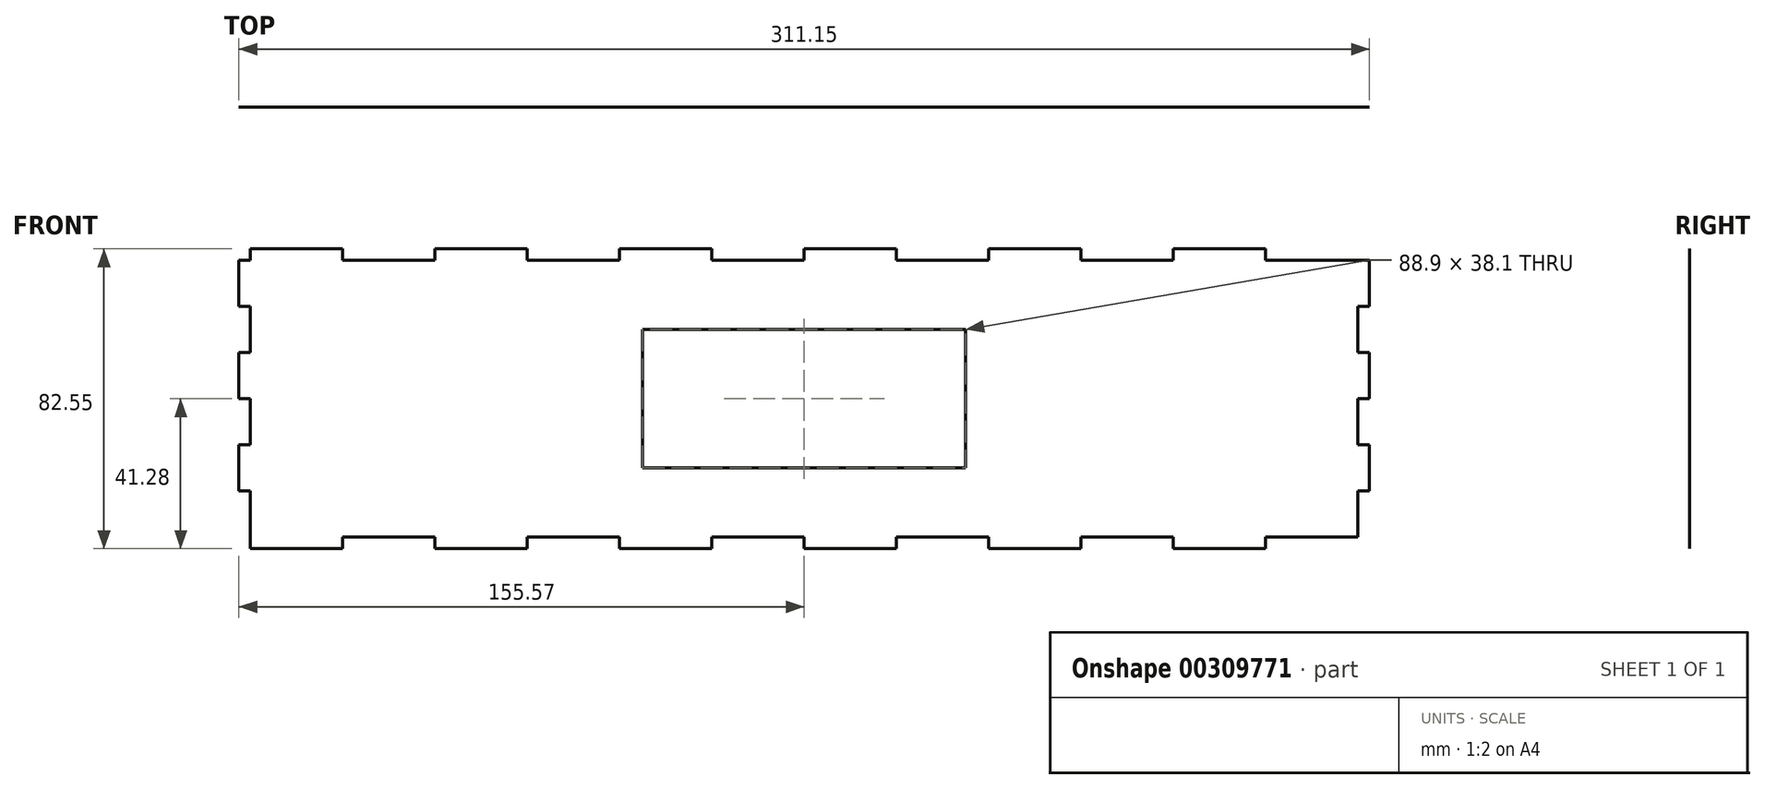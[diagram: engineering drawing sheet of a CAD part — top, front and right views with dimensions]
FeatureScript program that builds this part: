
annotation { "Feature Type Name" : "Feature", "Feature Type Description" : "" }
export const myFeature = defineFeature(function(context is Context, id is Id, definition is map)
    precondition{}
    {
        {
            var Q0;
            Q0=qCreatedBy(makeId("Front.planeOp"),FACE);
            var sketch = newSketch(context, id + "F0", { "sketchPlane" : qUnion([Q0])});
            skLineSegment(sketch, "E0.bottom", {"start": v(25.4, 0) * mm, "end": v(50.8, 0) * mm});
            skLineSegment(sketch, "E1.top", {"start": v(0, 3.18) * mm, "end": v(25.4, 3.18) * mm});
            skLineSegment(sketch, "E1.left", {"start": v(0, 0) * mm, "end": v(0, 3.18) * mm});
            skLineSegment(sketch, "E1.right", {"start": v(25.4, 0) * mm, "end": v(25.4, 3.18) * mm});
            skLineSegment(sketch, "E2.bottom", {"start": v(0, 0) * mm, "end": v(-3.17, 0) * mm});
            skLineSegment(sketch, "E2.top", {"start": v(0, -12.7) * mm, "end": v(-3.18, -12.7) * mm});
            skLineSegment(sketch, "E2.right", {"start": v(-3.18, 0) * mm, "end": v(-3.18, -12.7) * mm});
            skLineSegment(sketch, "E3.0.1.0", {"start": v(0, -25.4) * mm, "end": v(-3.17, -25.4) * mm});
            skLineSegment(sketch, "E3.0.1.1", {"start": v(-3.18, -25.4) * mm, "end": v(-3.18, -38.1) * mm});
            skLineSegment(sketch, "E3.0.1.2", {"start": v(0, -38.1) * mm, "end": v(-3.17, -38.1) * mm});
            skLineSegment(sketch, "E3.0.2.0", {"start": v(0, -50.8) * mm, "end": v(-3.17, -50.8) * mm});
            skLineSegment(sketch, "E3.0.2.1", {"start": v(-3.18, -50.8) * mm, "end": v(-3.18, -63.5) * mm});
            skLineSegment(sketch, "E3.0.2.2", {"start": v(0, -63.5) * mm, "end": v(-3.17, -63.5) * mm});
            skLineSegment(sketch, "E3.direction1", {"start": v(-3.17, 0) * mm, "end": v(0, 0) * mm, "construction": true});
            skLineSegment(sketch, "E3.direction2", {"start": v(-3.17, 0) * mm, "end": v(-3.17, -25.4) * mm, "construction": true});
            skLineSegment(sketch, "E4.1.0.0", {"start": v(50.8, 3.18) * mm, "end": v(76.2, 3.18) * mm});
            skLineSegment(sketch, "E4.1.0.1", {"start": v(50.8, 0) * mm, "end": v(50.8, 3.18) * mm});
            skLineSegment(sketch, "E4.1.0.2", {"start": v(76.2, 0) * mm, "end": v(76.2, 3.18) * mm});
            skLineSegment(sketch, "E4.2.0.0", {"start": v(101.6, 3.18) * mm, "end": v(127, 3.18) * mm});
            skLineSegment(sketch, "E4.2.0.1", {"start": v(101.6, 0) * mm, "end": v(101.6, 3.18) * mm});
            skLineSegment(sketch, "E4.2.0.2", {"start": v(127, 0) * mm, "end": v(127, 3.18) * mm});
            skLineSegment(sketch, "E4.3.0.0", {"start": v(152.4, 3.18) * mm, "end": v(177.8, 3.18) * mm});
            skLineSegment(sketch, "E4.3.0.1", {"start": v(152.4, 0) * mm, "end": v(152.4, 3.18) * mm});
            skLineSegment(sketch, "E4.3.0.2", {"start": v(177.8, 0) * mm, "end": v(177.8, 3.18) * mm});
            skLineSegment(sketch, "E4.4.0.0", {"start": v(203.2, 3.18) * mm, "end": v(228.6, 3.18) * mm});
            skLineSegment(sketch, "E4.4.0.1", {"start": v(203.2, 0) * mm, "end": v(203.2, 3.18) * mm});
            skLineSegment(sketch, "E4.4.0.2", {"start": v(228.6, 0) * mm, "end": v(228.6, 3.18) * mm});
            skLineSegment(sketch, "E4.5.0.0", {"start": v(254, 3.18) * mm, "end": v(279.4, 3.18) * mm});
            skLineSegment(sketch, "E4.5.0.1", {"start": v(254, 0) * mm, "end": v(254, 3.18) * mm});
            skLineSegment(sketch, "E4.5.0.2", {"start": v(279.4, 0) * mm, "end": v(279.4, 3.18) * mm});
            skLineSegment(sketch, "E4.direction1", {"start": v(0, 3.18) * mm, "end": v(50.8, 3.18) * mm, "construction": true});
            skLineSegment(sketch, "E5.trimOffspring", {"start": v(76.2, 0) * mm, "end": v(101.6, 0) * mm});
            skLineSegment(sketch, "E6.trimOffspring", {"start": v(127, 0) * mm, "end": v(152.4, 0) * mm});
            skLineSegment(sketch, "E7.trimOffspring", {"start": v(177.8, 0) * mm, "end": v(203.2, 0) * mm});
            skLineSegment(sketch, "E8.trimOffspring", {"start": v(228.6, 0) * mm, "end": v(254, 0) * mm});
            skLineSegment(sketch, "E9.trimOffspring", {"start": v(279.4, 0) * mm, "end": v(304.8, 0) * mm});
            skLineSegment(sketch, "E10.MirrorCS", {"start": v(307.98, 0) * mm, "end": v(307.98, -25.4) * mm, "construction": true});
            skLineSegment(sketch, "E11.MirrorCS", {"start": v(307.98, 0) * mm, "end": v(304.8, 0) * mm, "construction": true});
            skLineSegment(sketch, "E12.MirrorCS", {"start": v(304.8, -12.7) * mm, "end": v(307.98, -12.7) * mm});
            skLineSegment(sketch, "E13.MirrorCS", {"start": v(304.8, -25.4) * mm, "end": v(307.98, -25.4) * mm});
            skLineSegment(sketch, "E14.MirrorCS", {"start": v(307.98, -25.4) * mm, "end": v(307.98, -38.1) * mm});
            skLineSegment(sketch, "E15.MirrorCS", {"start": v(304.8, -38.1) * mm, "end": v(307.98, -38.1) * mm});
            skLineSegment(sketch, "E16.MirrorCS", {"start": v(304.8, -50.8) * mm, "end": v(307.98, -50.8) * mm});
            skLineSegment(sketch, "E17.MirrorCS", {"start": v(307.98, -50.8) * mm, "end": v(307.98, -63.5) * mm});
            skLineSegment(sketch, "E18.MirrorCS", {"start": v(304.8, -63.5) * mm, "end": v(307.98, -63.5) * mm});
            skLineSegment(sketch, "E19.trimOffspring", {"start": v(304.8, -38.1) * mm, "end": v(304.8, -50.8) * mm});
            skLineSegment(sketch, "E20.trimOffspring", {"start": v(304.8, -63.5) * mm, "end": v(304.8, -76.2) * mm});
            skLineSegment(sketch, "E21.trimOffspring", {"start": v(0, -38.1) * mm, "end": v(0, -50.8) * mm});
            skLineSegment(sketch, "E22.trimOffspring", {"start": v(0, -63.5) * mm, "end": v(0, -76.2) * mm});
            skLineSegment(sketch, "E23", {"start": v(0, -12.7) * mm, "end": v(0, -25.4) * mm});
            skLineSegment(sketch, "E24", {"start": v(304.8, -12.7) * mm, "end": v(304.8, -25.4) * mm});
            skLineSegment(sketch, "E25", {"start": v(307.98, 0) * mm, "end": v(307.98, -12.7) * mm});
            skLineSegment(sketch, "E26", {"start": v(307.98, 0) * mm, "end": v(304.8, 0) * mm});
            skLineSegment(sketch, "E27", {"start": v(25.4, -76.2) * mm, "end": v(50.8, -76.2) * mm});
            skLineSegment(sketch, "E28.MirrorCS", {"start": v(152.4, -79.38) * mm, "end": v(177.8, -79.38) * mm});
            skLineSegment(sketch, "E29.MirrorCS", {"start": v(203.2, -79.38) * mm, "end": v(228.6, -79.38) * mm});
            skLineSegment(sketch, "E30.MirrorCS", {"start": v(254, -79.38) * mm, "end": v(279.4, -79.38) * mm});
            skLineSegment(sketch, "E31.MirrorCS", {"start": v(101.6, -79.38) * mm, "end": v(127, -79.38) * mm});
            skLineSegment(sketch, "E32.MirrorCS", {"start": v(50.8, -79.38) * mm, "end": v(76.2, -79.38) * mm});
            skLineSegment(sketch, "E33.MirrorCS", {"start": v(25.4, -76.2) * mm, "end": v(25.4, -79.38) * mm});
            skLineSegment(sketch, "E34.MirrorCS", {"start": v(50.8, -76.2) * mm, "end": v(50.8, -79.38) * mm});
            skLineSegment(sketch, "E35.MirrorCS", {"start": v(76.2, -76.2) * mm, "end": v(76.2, -79.38) * mm});
            skLineSegment(sketch, "E36.MirrorCS", {"start": v(101.6, -76.2) * mm, "end": v(101.6, -79.38) * mm});
            skLineSegment(sketch, "E37.MirrorCS", {"start": v(127, -76.2) * mm, "end": v(127, -79.38) * mm});
            skLineSegment(sketch, "E38.MirrorCS", {"start": v(177.8, -76.2) * mm, "end": v(177.8, -79.38) * mm});
            skLineSegment(sketch, "E39.MirrorCS", {"start": v(152.4, -76.2) * mm, "end": v(152.4, -79.38) * mm});
            skLineSegment(sketch, "E40.MirrorCS", {"start": v(228.6, -76.2) * mm, "end": v(228.6, -79.38) * mm});
            skLineSegment(sketch, "E41.MirrorCS", {"start": v(203.2, -76.2) * mm, "end": v(203.2, -79.38) * mm});
            skLineSegment(sketch, "E42.MirrorCS", {"start": v(254, -76.2) * mm, "end": v(254, -79.38) * mm});
            skLineSegment(sketch, "E43.MirrorCS", {"start": v(279.4, -76.2) * mm, "end": v(279.4, -79.38) * mm});
            skLineSegment(sketch, "E44.MirrorCS", {"start": v(0, -76.2) * mm, "end": v(0, -79.38) * mm});
            skLineSegment(sketch, "E45", {"start": v(0, -79.38) * mm, "end": v(25.4, -79.38) * mm});
            skLineSegment(sketch, "E46.trimOffspring", {"start": v(76.2, -76.2) * mm, "end": v(101.6, -76.2) * mm});
            skLineSegment(sketch, "E47.trimOffspring", {"start": v(127, -76.2) * mm, "end": v(152.4, -76.2) * mm});
            skLineSegment(sketch, "E48.trimOffspring", {"start": v(177.8, -76.2) * mm, "end": v(203.2, -76.2) * mm});
            skLineSegment(sketch, "E49.trimOffspring", {"start": v(228.6, -76.2) * mm, "end": v(254, -76.2) * mm});
            skLineSegment(sketch, "E50.trimOffspring", {"start": v(279.4, -76.2) * mm, "end": v(304.8, -76.2) * mm});
            skSolve(sketch);
        }
        {
            var Q0;
            Q0=makeQuery(id+"F0.imprint","IMPRINT",FACE,{"disambiguationData":[TD([[makeQuery(id+"F0.imprint","IMPRINT",EDGE,{"derivedFrom":sQuery(id+"F0.wireOp",EDGE,"E0.bottom")}),-1.0]])]});
            var Q1;
            {var subQ4=sQuery(id+"F0.wireOp",EDGE,"E4.3.0.0");Q1=makeQuery(id+"F0.imprint","IMPRINT",FACE,{"disambiguationData":[TD([[makeQuery(id+"F0.imprint","IMPRINT",EDGE,{"derivedFrom":subQ4}),-1.0]])]});}
            var Q2;
            {var subQ6=sQuery(id+"F0.wireOp",EDGE,"E17.MirrorCS");Q2=makeQuery(id+"F0.imprint","IMPRINT",FACE,{"disambiguationData":[TD([[makeQuery(id+"F0.imprint","IMPRINT",EDGE,{"derivedFrom":subQ6}),-1.0]])]});}
            extrude(context, id + "F1", {"entities" : qUnion([Q0, Q1, Q2]), "depth" : 1 / 203.2 * mm});
        }
        {
            var Q0;
            Q0=makeQuery(id+"F1.opExtrude","CAP_FACE",FACE,{"disambiguationData":[OSD([sQuery(id+"F0.wireOp",EDGE,"E0.bottom"),sQuery(id+"F0.wireOp",EDGE,"E1.top"),sQuery(id+"F0.wireOp",EDGE,"E1.left"),sQuery(id+"F0.wireOp",EDGE,"E1.right"),sQuery(id+"F0.wireOp",EDGE,"E2.bottom"),sQuery(id+"F0.wireOp",EDGE,"E2.top"),sQuery(id+"F0.wireOp",EDGE,"E2.right"),sQuery(id+"F0.wireOp",EDGE,"E3.0.1.0"),sQuery(id+"F0.wireOp",EDGE,"E3.0.1.1"),sQuery(id+"F0.wireOp",EDGE,"E3.0.1.2"),sQuery(id+"F0.wireOp",EDGE,"E3.0.2.0"),sQuery(id+"F0.wireOp",EDGE,"E3.0.2.1"),sQuery(id+"F0.wireOp",EDGE,"E3.0.2.2"),sQuery(id+"F0.wireOp",EDGE,"E4.1.0.0"),sQuery(id+"F0.wireOp",EDGE,"E4.1.0.1"),sQuery(id+"F0.wireOp",EDGE,"E4.1.0.2"),sQuery(id+"F0.wireOp",EDGE,"E4.2.0.0"),sQuery(id+"F0.wireOp",EDGE,"E4.2.0.1"),sQuery(id+"F0.wireOp",EDGE,"E4.2.0.2"),sQuery(id+"F0.wireOp",EDGE,"E4.3.0.0"),sQuery(id+"F0.wireOp",EDGE,"E4.3.0.1"),sQuery(id+"F0.wireOp",EDGE,"E4.3.0.2"),sQuery(id+"F0.wireOp",EDGE,"E4.4.0.0"),sQuery(id+"F0.wireOp",EDGE,"E4.4.0.1"),sQuery(id+"F0.wireOp",EDGE,"E4.4.0.2"),sQuery(id+"F0.wireOp",EDGE,"E4.5.0.0"),sQuery(id+"F0.wireOp",EDGE,"E4.5.0.1"),sQuery(id+"F0.wireOp",EDGE,"E4.5.0.2"),sQuery(id+"F0.wireOp",EDGE,"E5.trimOffspring"),sQuery(id+"F0.wireOp",EDGE,"E6.trimOffspring"),sQuery(id+"F0.wireOp",EDGE,"E7.trimOffspring"),sQuery(id+"F0.wireOp",EDGE,"E8.trimOffspring"),sQuery(id+"F0.wireOp",EDGE,"E9.trimOffspring"),sQuery(id+"F0.wireOp",EDGE,"E12.MirrorCS"),sQuery(id+"F0.wireOp",EDGE,"E13.MirrorCS"),sQuery(id+"F0.wireOp",EDGE,"E14.MirrorCS"),sQuery(id+"F0.wireOp",EDGE,"E15.MirrorCS"),sQuery(id+"F0.wireOp",EDGE,"E16.MirrorCS"),sQuery(id+"F0.wireOp",EDGE,"E17.MirrorCS"),sQuery(id+"F0.wireOp",EDGE,"E18.MirrorCS"),sQuery(id+"F0.wireOp",EDGE,"E19.trimOffspring"),sQuery(id+"F0.wireOp",EDGE,"E20.trimOffspring"),sQuery(id+"F0.wireOp",EDGE,"E21.trimOffspring"),sQuery(id+"F0.wireOp",EDGE,"E22.trimOffspring"),sQuery(id+"F0.wireOp",EDGE,"E23"),sQuery(id+"F0.wireOp",EDGE,"E24"),sQuery(id+"F0.wireOp",EDGE,"E25"),sQuery(id+"F0.wireOp",EDGE,"E26"),sQuery(id+"F0.wireOp",EDGE,"E27"),sQuery(id+"F0.wireOp",EDGE,"E28.MirrorCS"),sQuery(id+"F0.wireOp",EDGE,"E29.MirrorCS"),sQuery(id+"F0.wireOp",EDGE,"E30.MirrorCS"),sQuery(id+"F0.wireOp",EDGE,"E31.MirrorCS"),sQuery(id+"F0.wireOp",EDGE,"E32.MirrorCS"),sQuery(id+"F0.wireOp",EDGE,"E33.MirrorCS"),sQuery(id+"F0.wireOp",EDGE,"E34.MirrorCS"),sQuery(id+"F0.wireOp",EDGE,"E35.MirrorCS"),sQuery(id+"F0.wireOp",EDGE,"E36.MirrorCS"),sQuery(id+"F0.wireOp",EDGE,"E37.MirrorCS"),sQuery(id+"F0.wireOp",EDGE,"E38.MirrorCS"),sQuery(id+"F0.wireOp",EDGE,"E39.MirrorCS"),sQuery(id+"F0.wireOp",EDGE,"E40.MirrorCS"),sQuery(id+"F0.wireOp",EDGE,"E41.MirrorCS"),sQuery(id+"F0.wireOp",EDGE,"E42.MirrorCS"),sQuery(id+"F0.wireOp",EDGE,"E43.MirrorCS"),sQuery(id+"F0.wireOp",EDGE,"E44.MirrorCS"),sQuery(id+"F0.wireOp",EDGE,"E45"),sQuery(id+"F0.wireOp",EDGE,"E46.trimOffspring"),sQuery(id+"F0.wireOp",EDGE,"E47.trimOffspring"),sQuery(id+"F0.wireOp",EDGE,"E48.trimOffspring"),sQuery(id+"F0.wireOp",EDGE,"E49.trimOffspring"),sQuery(id+"F0.wireOp",EDGE,"E50.trimOffspring")])],"isStart":false});
            var sketch = newSketch(context, id + "F2", { "sketchPlane" : qUnion([Q0])});
            skLineSegment(sketch, "E51.bottom", {"start": v(107.95, -19.05) * mm, "end": v(196.85, -19.05) * mm});
            skLineSegment(sketch, "E51.top", {"start": v(107.95, -57.15) * mm, "end": v(196.85, -57.15) * mm});
            skLineSegment(sketch, "E51.left", {"start": v(107.95, -19.05) * mm, "end": v(107.95, -57.15) * mm});
            skLineSegment(sketch, "E51.right", {"start": v(196.85, -19.05) * mm, "end": v(196.85, -57.15) * mm});
            skSolve(sketch);
        }
        {
            var Q0;
            Q0=makeQuery(id+"F2.imprint","IMPRINT",FACE,{"disambiguationData":[TD([[makeQuery(id+"F2.imprint","IMPRINT",EDGE,{"derivedFrom":sQuery(id+"F2.wireOp",EDGE,"E51.bottom")}),-1.0]])]});
            extrude(context, id + "F3", {"entities" : qUnion([Q0]), "operationType" : NewBodyOperationType.REMOVE, "oppositeDirection" : true, "depth" : 25.4 * mm});
        }
    });
